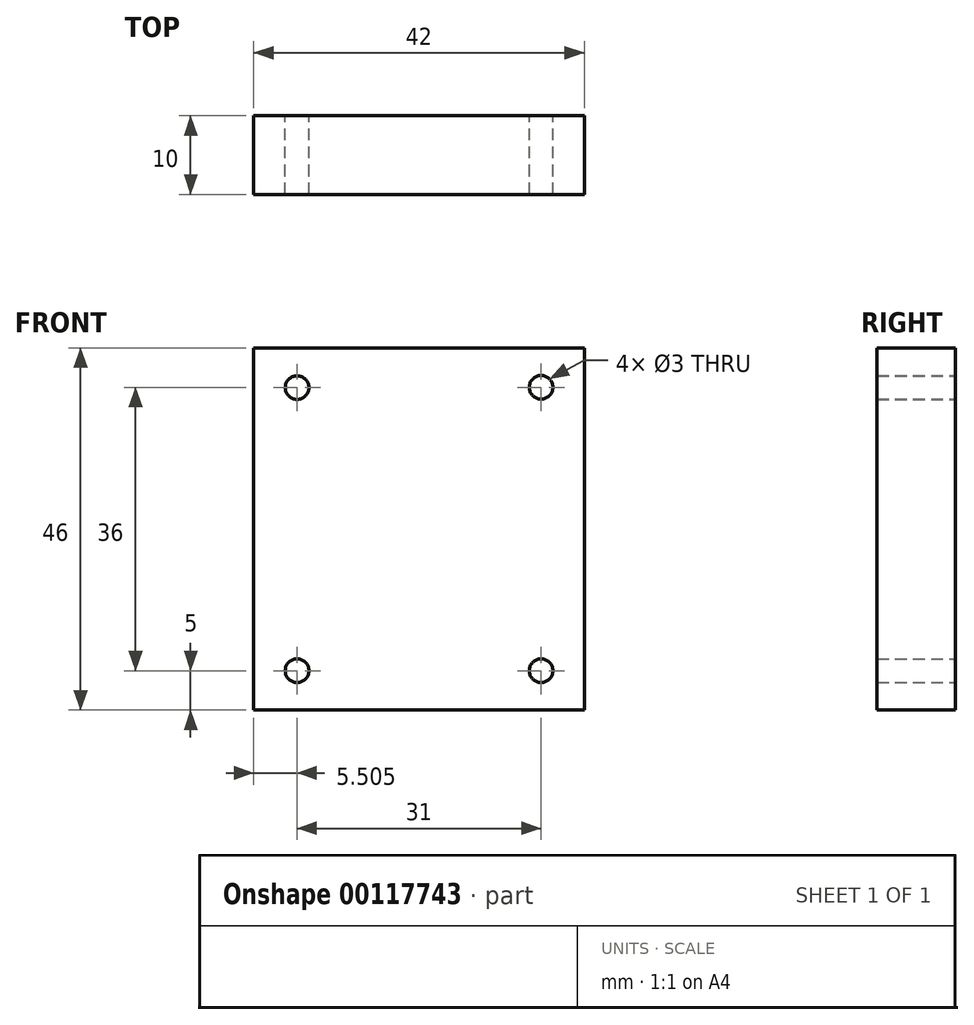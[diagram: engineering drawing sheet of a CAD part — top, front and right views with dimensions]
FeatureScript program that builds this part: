
annotation { "Feature Type Name" : "Feature", "Feature Type Description" : "" }
export const myFeature = defineFeature(function(context is Context, id is Id, definition is map)
    precondition{}
    {
        {
            var Q0;
            Q0=qCreatedBy(makeId("Front.planeOp"),FACE);
            var sketch = newSketch(context, id + "F0", { "sketchPlane" : qUnion([Q0])});
            skCircle(sketch, "E0", {"center": v(-50.7, 35.96) * mm, "radius": 1.5 * mm});
            skCircle(sketch, "E1", {"center": v(-19.7, 36) * mm, "radius": 1.5 * mm});
            skCircle(sketch, "E2", {"center": v(-19.7, 0) * mm, "radius": 1.5 * mm});
            skCircle(sketch, "E3", {"center": v(-50.7, 0) * mm, "radius": 1.5 * mm});
            skPoint(sketch, "E4.start.orphan", {"position": v(-50.7, 38) * mm});
            skPoint(sketch, "E5.start.orphan", {"position": v(-19.7, 38) * mm});
            skPoint(sketch, "E6.orphan", {"position": v(-17.7, 36) * mm});
            skPoint(sketch, "E7.start.orphan", {"position": v(-52.7, 0) * mm});
            skPoint(sketch, "E8.trimOffspring.end.orphan", {"position": v(-17.7, 0) * mm});
            skLineSegment(sketch, "E9.bottom", {"start": v(-56.2, -5) * mm, "end": v(-14.2, -5) * mm});
            skLineSegment(sketch, "E9.top", {"start": v(-56.2, 41) * mm, "end": v(-14.2, 41) * mm});
            skLineSegment(sketch, "E9.left", {"start": v(-56.2, -5) * mm, "end": v(-56.2, 41) * mm});
            skLineSegment(sketch, "E9.right", {"start": v(-14.2, -5) * mm, "end": v(-14.2, 41) * mm});
            skPoint(sketch, "E9.middle", {"position": v(-35.2, 18) * mm});
            skPoint(sketch, "E10.orphan", {"position": v(-17.7, 18) * mm});
            skPoint(sketch, "E11.end.orphan", {"position": v(-35.2, -2) * mm});
            skPoint(sketch, "E12.end.orphan", {"position": v(-52.7, 18) * mm});
            skPoint(sketch, "E13.orphan", {"position": v(-35.2, 38) * mm});
            skPoint(sketch, "E14.bottom.start.orphan", {"position": v(-52.7, 38) * mm});
            skPoint(sketch, "E15.orphan", {"position": v(-52.7, -2) * mm});
            skPoint(sketch, "E16.orphan", {"position": v(-17.7, -2) * mm});
            skPoint(sketch, "E17.trimOffspring.end.orphan", {"position": v(-17.7, 38) * mm});
            skSolve(sketch);
        }
        {
            var Q0;
            Q0=makeQuery(id+"F0.imprint","IMPRINT",FACE,{"disambiguationData":[TD([[makeQuery(id+"F0.imprint","IMPRINT",EDGE,{"derivedFrom":sQuery(id+"F0.wireOp",EDGE,"E0")}),-1.0]])]});
            extrude(context, id + "F1", {"entities" : qUnion([Q0]), "depth" : 10 * mm});
        }
    });
